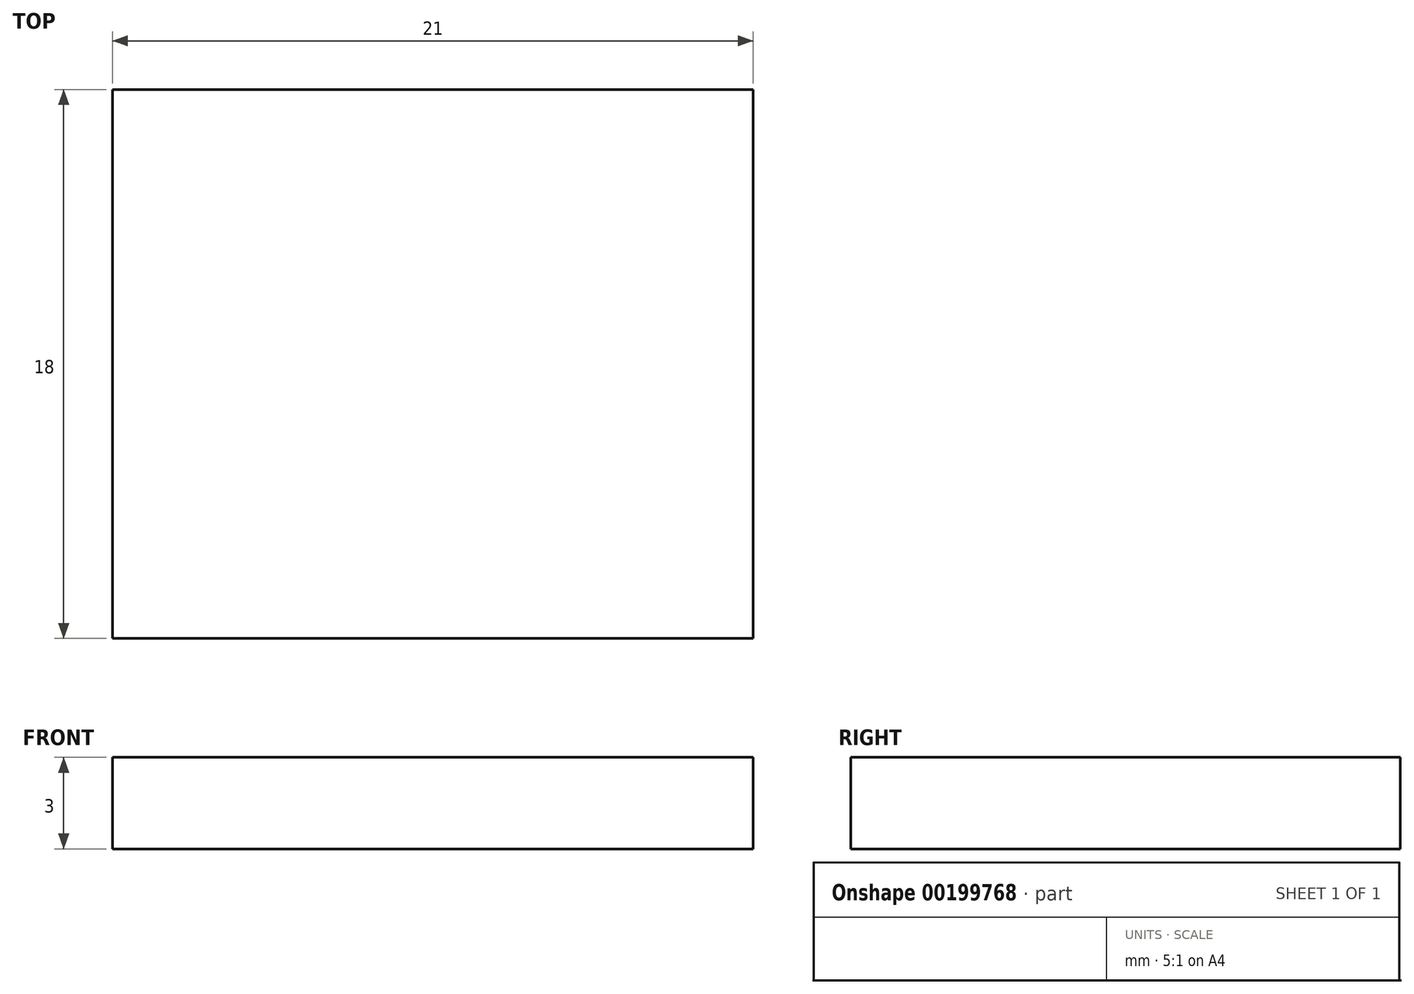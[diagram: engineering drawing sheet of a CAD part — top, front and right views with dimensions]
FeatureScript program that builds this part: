
annotation { "Feature Type Name" : "Feature", "Feature Type Description" : "" }
export const myFeature = defineFeature(function(context is Context, id is Id, definition is map)
    precondition{}
    {
        {
            var Q0;
            Q0=qCreatedBy(makeId("Top.planeOp"),FACE);
            var sketch = newSketch(context, id + "F0", { "sketchPlane" : qUnion([Q0])});
            skLineSegment(sketch, "E0.bottom", {"start": v(0, 0) * mm, "end": v(21, 0) * mm});
            skLineSegment(sketch, "E0.top", {"start": v(0, 18) * mm, "end": v(21, 18) * mm});
            skLineSegment(sketch, "E0.left", {"start": v(0, 0) * mm, "end": v(0, 18) * mm});
            skLineSegment(sketch, "E0.right", {"start": v(21, 0) * mm, "end": v(21, 18) * mm});
            skSolve(sketch);
        }
        {
            var Q0;
            Q0=makeQuery(id+"F0.imprint","IMPRINT",FACE,{"disambiguationData":[TD([[makeQuery(id+"F0.imprint","IMPRINT",EDGE,{"derivedFrom":sQuery(id+"F0.wireOp",EDGE,"E0.bottom")}),1.0]])]});
            extrude(context, id + "F1", {"entities" : qUnion([Q0]), "depth" : 3 * mm});
        }
    });
